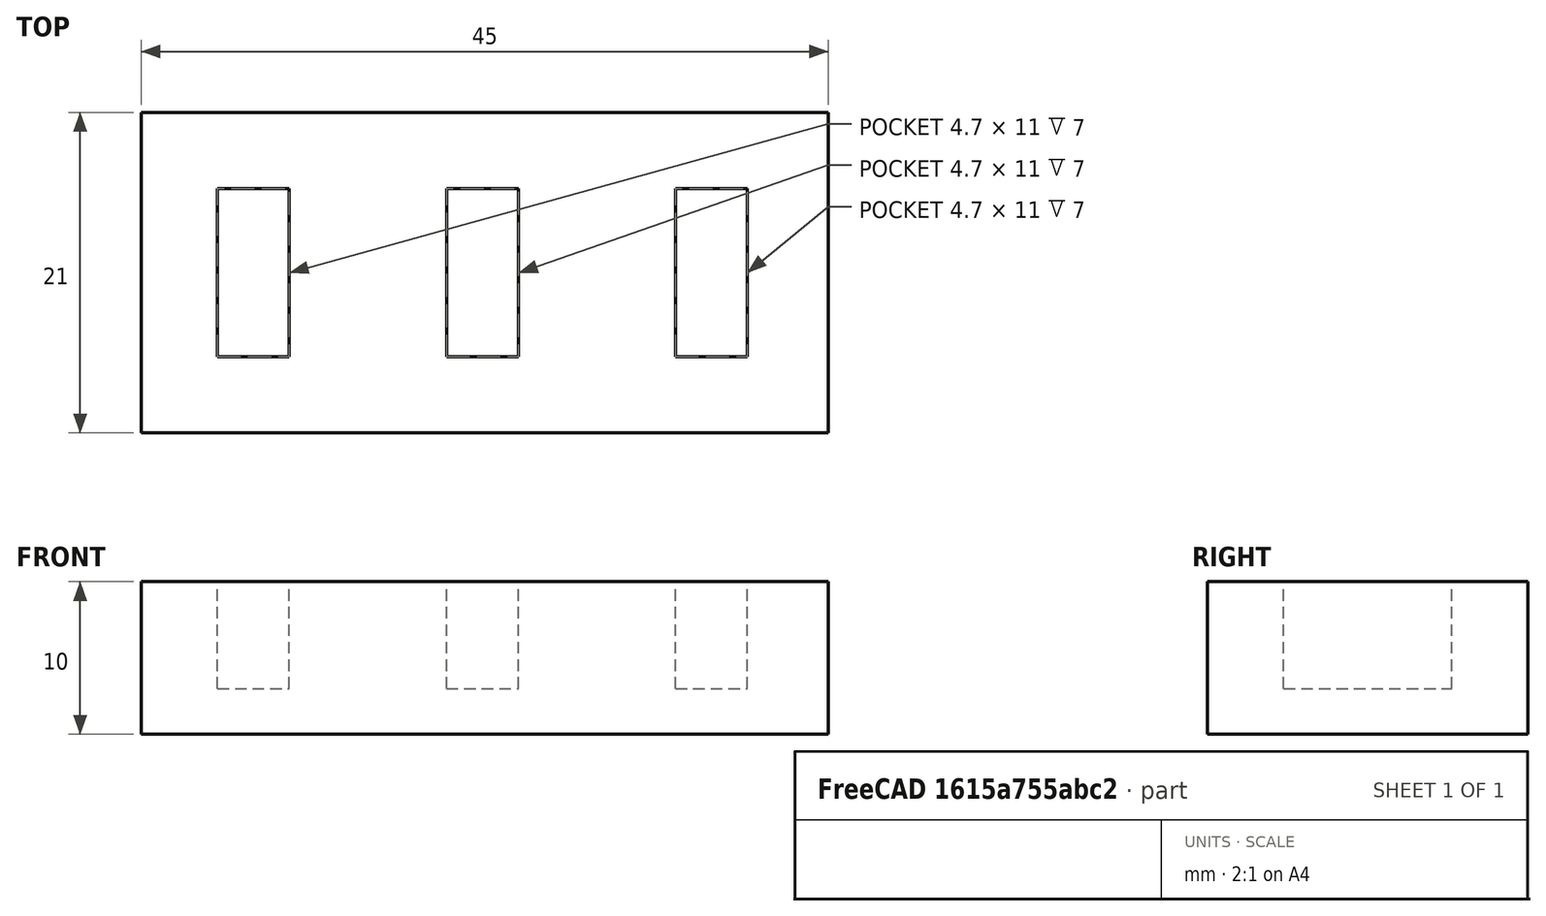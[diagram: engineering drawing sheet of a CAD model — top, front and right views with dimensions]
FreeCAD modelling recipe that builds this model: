
FCSTD DOCUMENT  (FreeCAD 0.21R33771 (Git))
Label: OJT1_T08P01_portapendrives
License: All rights reserved
LicenseURL: http://en.wikipedia.org/wiki/All_rights_reserved
objects: Part::Box×4, Part::MultiFuse×1, Part::Cut×1
note: 6 computed .brp shape members not serialized (recipe doc carries the construction recipe); baked Part::Feature solids carry a one-line shape summary decoded from their .brp

FEATURE [Part::Box] Box  label="ranura1"
  AttacherType = Attacher::AttachEngine3D
  Height = 12
  Length = 4.7
  Placement = pos=(5,5,0) rot=(0,0,1;0rad)
  Width = 11
FEATURE [Part::Box] Box001  label="ranura002"
  AttacherType = Attacher::AttachEngine3D
  Height = 12
  Length = 4.7
  Placement = pos=(20,5,0) rot=(0,0,1;0rad)
  Width = 11
FEATURE [Part::Box] Box002  label="ranura003"
  AttacherType = Attacher::AttachEngine3D
  Height = 12
  Length = 4.7
  Placement = pos=(35,5,0) rot=(0,0,1;0rad)
  Width = 11
FEATURE [Part::MultiFuse] Fusion  label="ranures"
  Placement = pos=(0,0,3) rot=(0,0,1;0rad)
  Refine = true
  Shapes = -> [Box,Box001,Box002]
FEATURE [Part::Box] Box003  label="base"
  AttacherType = Attacher::AttachEngine3D
  Height = 10
  Length = 45
  Width = 21
FEATURE [Part::Cut] Cut  label="porta_pendrives"
  Base = -> Box003
  Refine = true
  Tool = -> Fusion
